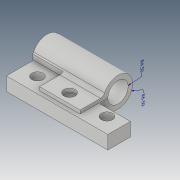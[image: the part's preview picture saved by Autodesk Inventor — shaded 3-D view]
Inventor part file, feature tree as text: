
AUTODESK INVENTOR PART (.ipt)
format: ipt  version: 2019 (Build 230136000, 136)  size: 240,128 bytes
history: native  units: mm
features: extrude x11, sketch x9, plane x4, other x3, fillet x2, move_body x2, direct_edit x1, projected_geometry x1
ambient origin geometry x8: Origin, YZ Plane, XZ Plane, XY Plane, X Axis, Y Axis, Z Axis, Center Point
bodies: Solid1 (feature_tree)
feature tree (33):
  other  "Annotations"
  extrude  "Extrusion1"  Depth=45.0mm
  extrude  "Extrusion4"  Depth=5.0mm
  fillet  "Fillet1"  Radius=11.0mm
  extrude  "Extrusion5"  Depth=23.0mm
  plane  "Work Plane1"
  extrude  "Extrusion6"  Depth=10.0mm
  direct_edit  "Direct Edit1"
  extrude  "Extrusion7"  Depth=12.0mm
  fillet  "Fillet2"  Radius=5.0mm
  plane  "Work Plane5"
  extrude  "Extrusion8"  Depth=5.0mm
  plane  "Work Plane6"
  extrude  "Extrusion9"  Depth=17.8mm
  sketch  "Sketch12"  dims[d34=5.0mm d35=17.8mm]
  extrude  "Extrusion12"  Depth=8.0mm
  extrude  "Extrusion13"  Depth=4.5mm
  extrude  "Extrusion15"  Depth=4.5mm
  plane  "Work Plane7"
  extrude  "Extrusion16"  Depth=4.5mm TaperAngle=0.0deg
  sketch  "Sketch1"  dims[d0=6.0mm d1=0.0mm d4=45.0mm]
  sketch  "Sketch5"  dims[d5=5.0mm d6=5.0mm d7=11.0mm]
  sketch  "Sketch6"  dims[d8=11.0mm d9=23.0mm]
  sketch  "Sketch7"  dims[d10=10.0mm d20=13.0mm]
  sketch  "Sketch8"  dims[d24=3.0mm d25=0.0mm d26=12.0mm d27=5.0mm]
  sketch  "Sketch10"  dims[d28=3.0mm d29=0.0mm d33=5.0mm]
  projected_geometry  "Projected Loop2"
  sketch  "Sketch13"  dims[d36=8.0mm d37=17.8mm]
  sketch  "Sketch14"  dims[d38=7.1mm d39=30.8mm d40=7.1mm d41=3.0mm d42=0.0mm d46=0.0mm d47=0.0mm d48=-2.5mm d49=0.0mm d50=0.0mm d51=-2.5mm d52=18.0mm d53=11.0mm d54=2.0mm d55=0.0mm d56=2.0mm d57=0.0mm d58=0.5mm d59=0.0mm d60=0.0mm d61=7.25mm d62=0.0mm d68=5.0mm d69=7.25mm d70=0.0mm d72=2.0mm d73=10.0mm d74=0.0mm d80=10.0mm d81=0.0mm d82=15.0mm d83=3.0mm d88=-6.0mm d89=7.5mm d90=3.15mm d91=0.0mm d84=49.911908mm d85=6.5mm d86=52.109261mm d87=4.5mm]
  move_body  "Move1"
  move_body  "Move2"
  other  "Radial Dimension 1"
  other  "Radial Dimension 2"
